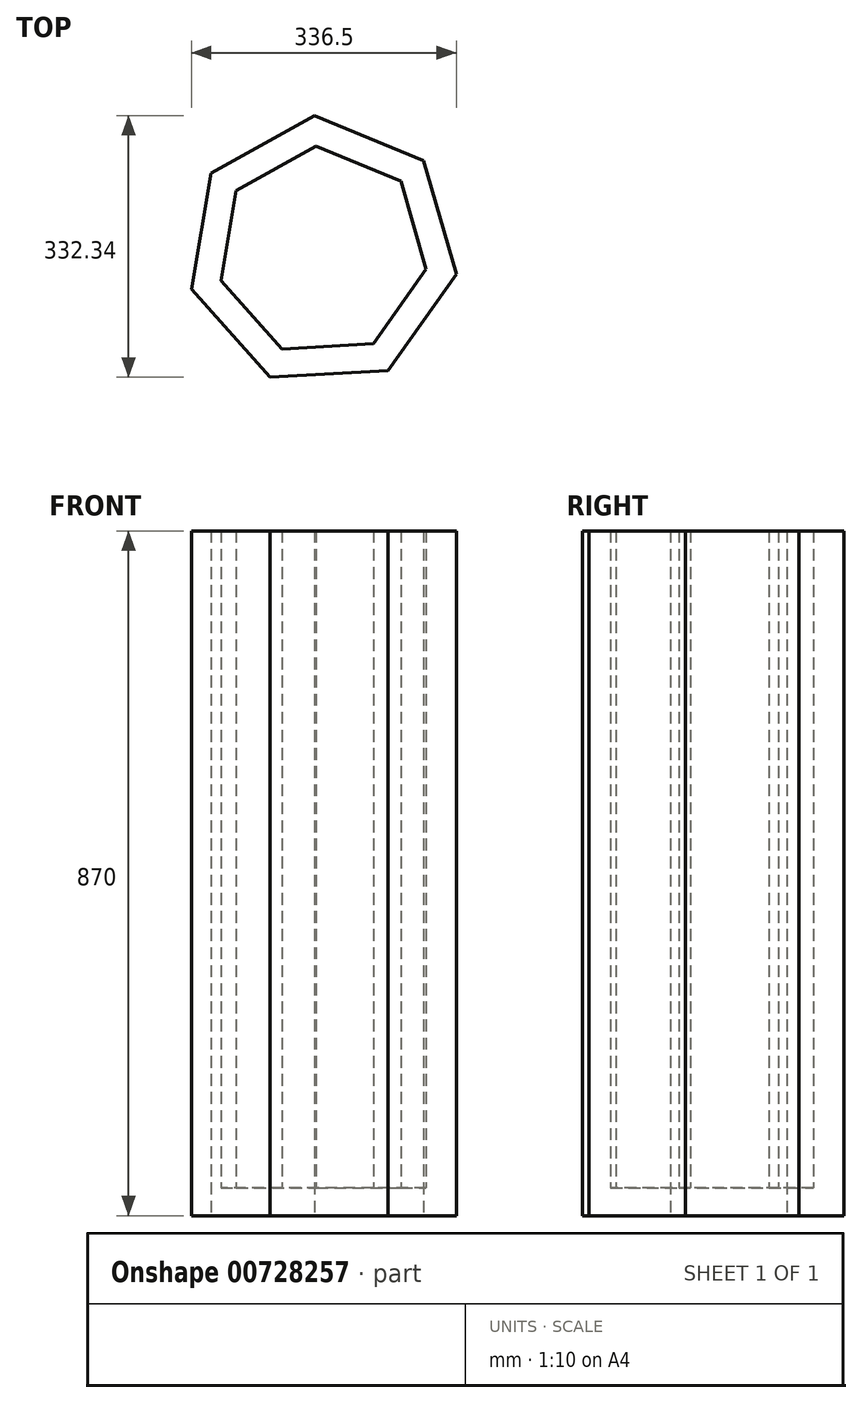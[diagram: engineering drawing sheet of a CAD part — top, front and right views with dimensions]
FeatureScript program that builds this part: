
annotation { "Feature Type Name" : "Feature", "Feature Type Description" : "" }
export const myFeature = defineFeature(function(context is Context, id is Id, definition is map)
    precondition{}
    {
        {
            var Q0;
            Q0=qCreatedBy(makeId("Top.planeOp"),FACE);
            var sketch = newSketch(context, id + "F0", { "sketchPlane" : qUnion([Q0])});
            skCircle(sketch, "E0.cCircle", {"center": v(0, 0) * mm, "radius": 155.74 * mm, "construction": true});
            skLineSegment(sketch, "E0.0", {"start": v(-141.07, 99.9) * mm, "end": v(-9.85, 172.58) * mm});
            skLineSegment(sketch, "E0.1", {"start": v(-9.85, 172.58) * mm, "end": v(128.78, 115.3) * mm});
            skLineSegment(sketch, "E0.2", {"start": v(128.78, 115.3) * mm, "end": v(170.44, -28.8) * mm});
            skLineSegment(sketch, "E0.3", {"start": v(170.44, -28.8) * mm, "end": v(83.76, -151.21) * mm});
            skLineSegment(sketch, "E0.4", {"start": v(83.76, -151.21) * mm, "end": v(-66, -159.76) * mm});
            skLineSegment(sketch, "E0.5", {"start": v(-66, -159.76) * mm, "end": v(-166.06, -48) * mm});
            skLineSegment(sketch, "E0.6", {"start": v(-166.06, -48) * mm, "end": v(-141.07, 99.9) * mm});
            skPoint(sketch, "E0.0.midPoint", {"position": v(-75.46, 136.24) * mm});
            skSolve(sketch);
        }
        {
            var Q0;
            Q0=makeQuery(id+"F0.imprint","IMPRINT",FACE,{"disambiguationData":[TD([[makeQuery(id+"F0.imprint","IMPRINT",EDGE,{"derivedFrom":sQuery(id+"F0.wireOp",EDGE,"E0.0")}),-1.0]])]});
            extrude(context, id + "F1", {"entities" : qUnion([Q0]), "depth" : 870 * mm, "offsetDistance" : 25 * mm});
        }
        {
            var Q0;
            Q0=makeQuery(id+"F1.opExtrude","CAP_FACE",FACE,{"disambiguationData":[OSD([sQuery(id+"F0.wireOp",EDGE,"E0.0"),sQuery(id+"F0.wireOp",EDGE,"E0.1"),sQuery(id+"F0.wireOp",EDGE,"E0.2"),sQuery(id+"F0.wireOp",EDGE,"E0.3"),sQuery(id+"F0.wireOp",EDGE,"E0.4"),sQuery(id+"F0.wireOp",EDGE,"E0.5"),sQuery(id+"F0.wireOp",EDGE,"E0.6")])],"isStart":false});
            shell(context, id + "F2", {"entities" : qUnion([Q0]), "thickness" : 35 * mm});
        }
    });
